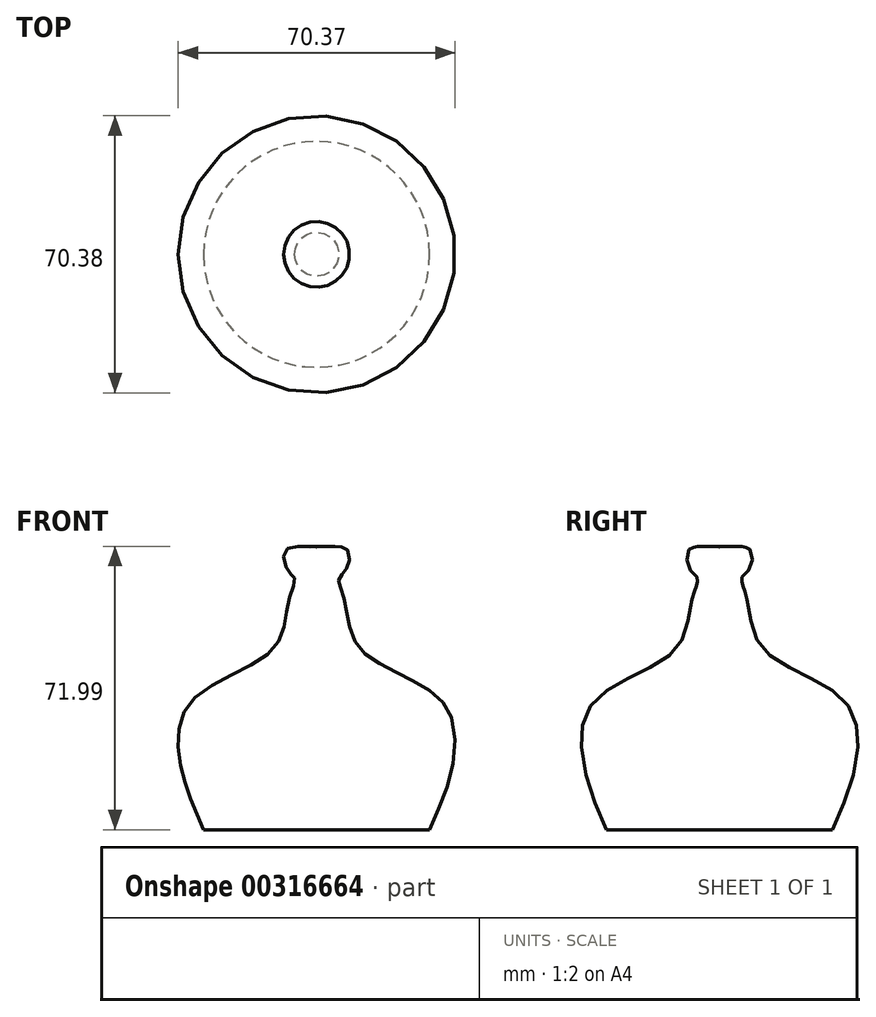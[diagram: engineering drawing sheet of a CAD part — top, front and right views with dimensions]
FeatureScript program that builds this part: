
annotation { "Feature Type Name" : "Feature", "Feature Type Description" : "" }
export const myFeature = defineFeature(function(context is Context, id is Id, definition is map)
    precondition{}
    {
        {
            var Q0;
            Q0=qCreatedBy(makeId("Front.planeOp"),FACE);
            var sketch = newSketch(context, id + "F0", { "sketchPlane" : qUnion([Q0])});
            skLineSegment(sketch, "E0", {"start": v(0, 55.3) * mm, "end": v(0, -15.53) * mm, "construction": true});
            skSolve(sketch);
        }
        {
            var Q0;
            Q0=qCreatedBy(makeId("Front.planeOp"),FACE);
            var sketch = newSketch(context, id + "F1", { "sketchPlane" : qUnion([Q0])});
            skLineSegment(sketch, "E1", {"start": v(0, -15.53) * mm, "end": v(-28.7, -15.53) * mm});
            skFitSpline(sketch, "E2", {"points": [v(-28.7, -15.53) * mm, v(-34.36, 0) * mm, v(-31.77, 17.18) * mm, v(-11.3, 30.12) * mm, v(-7.06, 42.6) * mm, v(-5.65, 48.48) * mm, v(-7.06, 49.89) * mm, v(-8, 55.3) * mm, v(0, 56) * mm], "startDerivative": vector(-42, 93.6) * mm, "endDerivative": vector(95.27, -13.05) * mm});
            skLineSegment(sketch, "E3", {"start": v(0, 56) * mm, "end": v(0, -15.53) * mm});
            skSolve(sketch);
        }
        {
            var Q0;
            Q0 = qSketchRegion(id + "F0", true);
            var Q1;
            Q1 = qSketchRegion(id + "F1", true);
            var Q2;
            Q2=sQuery(id+"F1.wireOp",EDGE,"E3");
            revolve(context, id + "F2", {"entities" : qUnion([Q0, Q1]), "axis" : qUnion([Q2]), "revolveType" : RevolveType.FULL});
        }
    });
